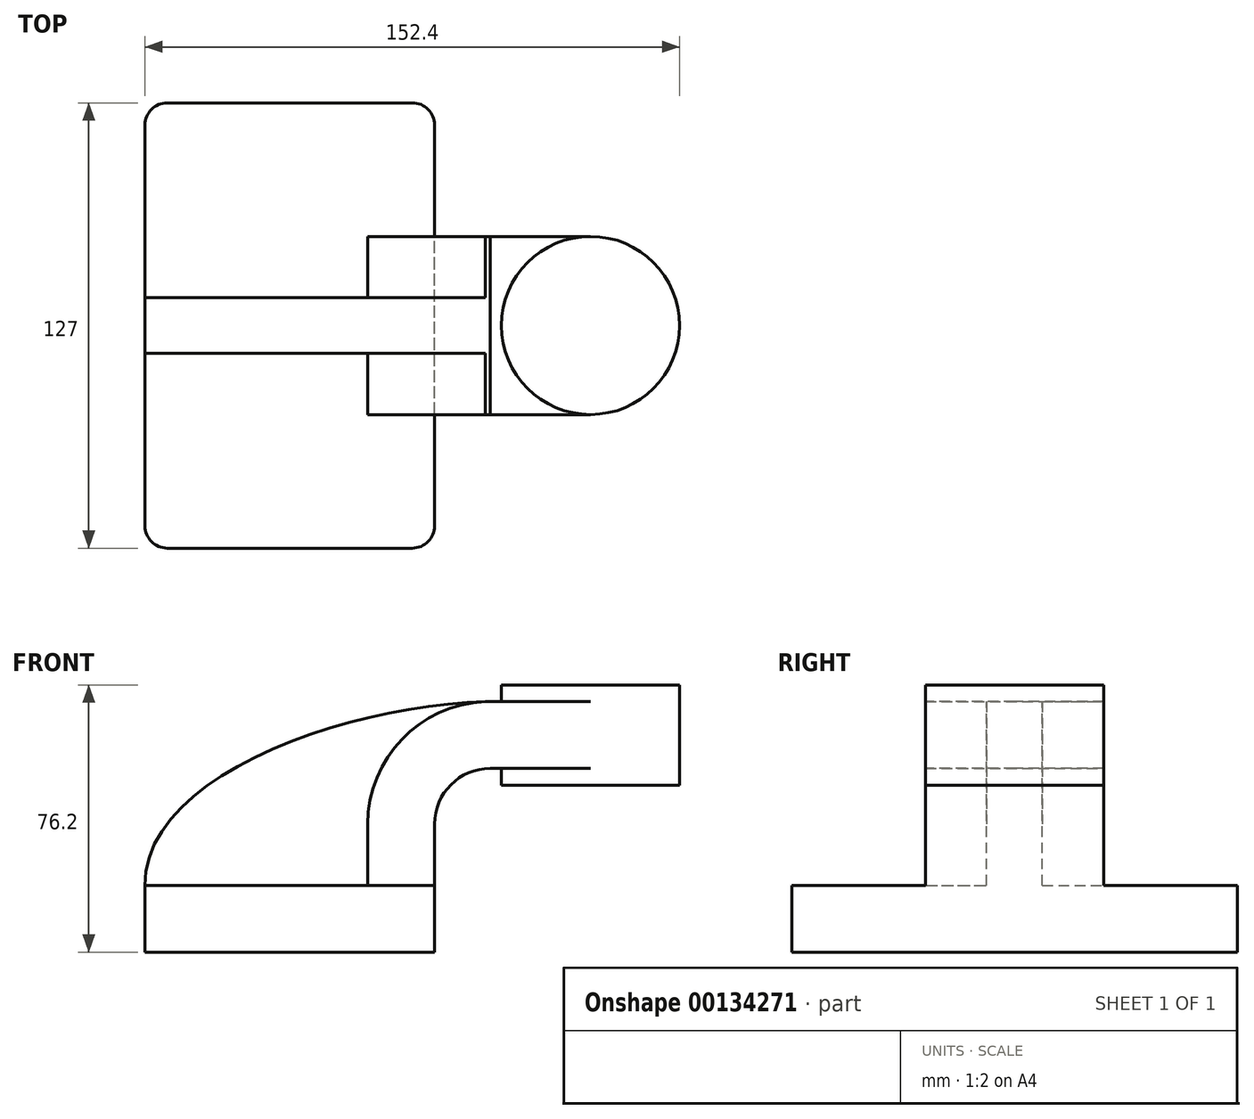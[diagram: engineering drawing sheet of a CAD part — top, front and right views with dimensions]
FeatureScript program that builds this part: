
annotation { "Feature Type Name" : "Feature", "Feature Type Description" : "" }
export const myFeature = defineFeature(function(context is Context, id is Id, definition is map)
    precondition{}
    {
        {
            var Q0;
            Q0=qCreatedBy(makeId("Front.planeOp"),FACE);
            var sketch = newSketch(context, id + "F0", { "sketchPlane" : qUnion([Q0])});
            skLineSegment(sketch, "E0.bottom", {"start": v(39.92, 21.45) * mm, "end": v(-42.63, 21.45) * mm});
            skLineSegment(sketch, "E0.top", {"start": v(39.92, 40.5) * mm, "end": v(-42.63, 40.5) * mm});
            skLineSegment(sketch, "E0.left", {"start": v(39.92, 21.45) * mm, "end": v(39.92, 40.5) * mm});
            skLineSegment(sketch, "E0.right", {"start": v(-42.63, 21.45) * mm, "end": v(-42.63, 40.5) * mm});
            skPoint(sketch, "E0.middle", {"position": v(-1.35, 30.97) * mm});
            skLineSegment(sketch, "E1.bottom", {"start": v(109.77, 69.07) * mm, "end": v(58.97, 69.07) * mm});
            skLineSegment(sketch, "E1.top", {"start": v(109.77, 97.65) * mm, "end": v(58.97, 97.65) * mm});
            skLineSegment(sketch, "E1.left", {"start": v(109.77, 69.07) * mm, "end": v(109.77, 97.65) * mm});
            skLineSegment(sketch, "E1.right", {"start": v(58.97, 69.07) * mm, "end": v(58.97, 97.65) * mm});
            skPoint(sketch, "E1.middle", {"position": v(84.37, 83.36) * mm});
            skLineSegment(sketch, "E2", {"start": v(39.92, 40.5) * mm, "end": v(39.92, 57.97) * mm});
            skArc(sketch, "E3", {"start": v(39.92, 57.97) * mm, "mid": v(44.57, 69.2) * mm, "end": v(55.8, 73.85) * mm});
            skLineSegment(sketch, "E4", {"start": v(55.8, 73.85) * mm, "end": v(84.37, 73.85) * mm});
            skLineSegment(sketch, "E5.0", {"start": v(55.8, 92.9) * mm, "end": v(84.37, 92.9) * mm});
            skArc(sketch, "E5.1", {"start": v(20.87, 57.97) * mm, "mid": v(31.1, 82.67) * mm, "end": v(55.8, 92.9) * mm});
            skLineSegment(sketch, "E5.2", {"start": v(20.87, 40.5) * mm, "end": v(20.87, 57.97) * mm});
            skLineSegment(sketch, "E6", {"start": v(84.37, 69.07) * mm, "end": v(84.37, 97.65) * mm});
            skFitSpline(sketch, "E7", {"points": [v(-42.63, 40.5) * mm, v(55.8, 92.9) * mm], "startDerivative": vector(-0.61, 95.77) * mm, "endDerivative": vector(117.65, 1.75) * mm});
            skSolve(sketch);
        }
        {
            var Q0;
            Q0=makeQuery(id+"F0.imprint","IMPRINT",FACE,{"disambiguationData":[TD([[makeQuery(id+"F0.imprint","IMPRINT",EDGE,{"derivedFrom":sQuery(id+"F0.wireOp",EDGE,"E0.bottom")}),-1.0]])]});
            extrude(context, id + "F1", {"entities" : qUnion([Q0]), "endBound" : BoundingType.SYMMETRIC, "depth" : 127 * mm});
        }
        {
            var Q0;
            {var subQ1=sQuery(id+"F0.wireOp",EDGE,"E2");Q0=makeQuery(id+"F0.imprint","IMPRINT",FACE,{"disambiguationData":[TD([[makeQuery(id+"F0.imprint","IMPRINT",EDGE,{"derivedFrom":subQ1}),1.0]])]});}
            var Q1;
            {var subQ0=sQuery(id+"F0.wireOp",EDGE,"E4");var subQ1=sQuery(id+"F0.wireOp",EDGE,"E1.right");var subQ2=makeQuery(id+"F0.imprint","INTERSECT",VERTEX,{"derivedFrom":[subQ1,subQ0]});Q1=makeQuery(id+"F0.imprint","IMPRINT",FACE,{"disambiguationData":[TD([[makeQuery(id+"F0.imprint","IMPRINT",EDGE,{"disambiguationData":[TD([[subQ2,-1.0]])],"derivedFrom":subQ1}),-1.0]])]});}
            extrude(context, id + "F2", {"entities" : qUnion([Q0, Q1]), "operationType" : NewBodyOperationType.ADD, "endBound" : BoundingType.SYMMETRIC, "depth" : 50.8 * mm});
        }
        {
            var Q0;
            {var subQ3=sQuery(id+"F0.wireOp",EDGE,"E5.2");Q0=makeQuery(id+"F0.imprint","IMPRINT",FACE,{"disambiguationData":[TD([[makeQuery(id+"F0.imprint","IMPRINT",EDGE,{"derivedFrom":subQ3}),1.0]])]});}
            extrude(context, id + "F3", {"entities" : qUnion([Q0]), "operationType" : NewBodyOperationType.ADD, "endBound" : BoundingType.SYMMETRIC, "depth" : 15.88 * mm});
        }
        {
            var Q0;
            {var subQ0=sQuery(id+"F0.wireOp",EDGE,"E1.left");Q0=makeQuery(id+"F0.imprint","IMPRINT",FACE,{"disambiguationData":[TD([[makeQuery(id+"F0.imprint","IMPRINT",EDGE,{"derivedFrom":subQ0}),1.0]])]});}
            var Q1;
            Q1=sQuery(id+"F0.wireOp",EDGE,"E6");
            revolve(context, id + "F4", {"operationType" : NewBodyOperationType.ADD, "entities" : qUnion([Q0]), "axis" : qUnion([Q1]), "revolveType" : RevolveType.FULL});
        }
        {
            var Q0;
            Q0=makeQuery(id+"F1.opExtrude","CAP_EDGE",EDGE,{"disambiguationData":[OSD([sQuery(id+"F0.wireOp",EDGE,"E0.left")])],"isStart":true});
            var Q1;
            Q1=makeQuery(id+"F1.opExtrude","CAP_EDGE",EDGE,{"disambiguationData":[OSD([sQuery(id+"F0.wireOp",EDGE,"E0.right")])],"isStart":false});
            var Q2;
            Q2=makeQuery(id+"F1.opExtrude","CAP_EDGE",EDGE,{"disambiguationData":[OSD([sQuery(id+"F0.wireOp",EDGE,"E0.left")])],"isStart":false});
            var Q3;
            Q3=makeQuery(id+"F1.opExtrude","CAP_EDGE",EDGE,{"disambiguationData":[OSD([sQuery(id+"F0.wireOp",EDGE,"E0.right")])],"isStart":true});
            fillet(context, id + "F5", {"entities" : qUnion([Q0, Q1, Q2, Q3]), "radius" : 6.35 * mm, "tangentPropagation" : true, "allowEdgeOverflow" : false});
        }
    });
